# Revit family: Plumbing_Drainage_AXOR_42526XXX-AXOR-Drain-Finish-set-shower-dr_NEW
name_source: partatom
category: Plumbing Fixtures
revit_build: Autodesk Revit 2018 (Build: 20170223_1515(x64)
units: mm (PartAtom-declared; Revit-internal decimal feet)

## family parameters
Cut with Voids When Loaded = Yes
Host = Face
OmniClass Number = 23.31.17.29
OmniClass Title = Shower Drains
Part Type = Normal
Room Calculation Point = No
Round Connector Dimension = Use Diameter
Shared = No

## types (13) — shared parameters
BIMobject category = Drainage
Default Elevation = 1219 mm
Description = AXOR Drain Finish set shower drain 800 for wall mounting
Design country = Germany
Edition number = 1
IFC Classification = Sanitary Terminal
Manufacturer = AXOR
Manufacturer country = Germany
Manufacturer name = AXOR
Material 1 = AXOR - Plastic - Dark Grey
Material 2 = AXOR - Plastic - Grey
Model = 42526XXX
OmniClass Code = 23-31 17 29
OmniClass Description = Shower Drains
Product Guid = 91c5bfd3-e536-4622-aa0f-144d5b81a230
Product SKU = 42526XXX
Product data url = https://bimobject.com
Product name = 42526XXX AXOR Drain Finish set shower drain 800 for wall mounting
Product url = https://www.axor-design.com
QR code = https://bimobject.com
URL = https://www.axor-design.com

## per-type parameters (varying)
| type | Material 3 |
| 800 Stainless Steel Optic | AXOR - Metal - 800 Stainless Steel Optic |
| 300 Polished Red Gold | AXOR - Metal - 300 Polished Red Gold |
| 990 Polished Gold Optic | AXOR - Metal - 990 Polished Gold Optic |
| 330 Polished Black Chrome | AXOR - Metal - 330 Polished Black Chrome |
| 700 Matte White | AXOR - Metal - 700 Matte White |
| 670 Matte Black | AXOR - Metal - 670 Matte Black |
| 310 Brushed Red Gold | AXOR - Metal - 310 Brushed Red Gold |
| 820 Brushed Nickel | AXOR - Metal - 820 Brushed Nickel |
| 250 Brushed Gold Optic | AXOR - Metal - 250 Brushed Gold Optic |
| 140 Brushed Bronze | AXOR - Metal - 140 Brushed Bronze |
| 950 Brushed Brass | AXOR - Metal - 950 Brushed Brass |
| 340 Brushed Black Chrome | AXOR - Metal - 340 Brushed Black Chrome |
| 000 Chrome | AXOR - Metal - 000 Chrome |

## geometry (parser evidence)
native form markers: Sweep x6
no freeform markers — native parametric forms only
